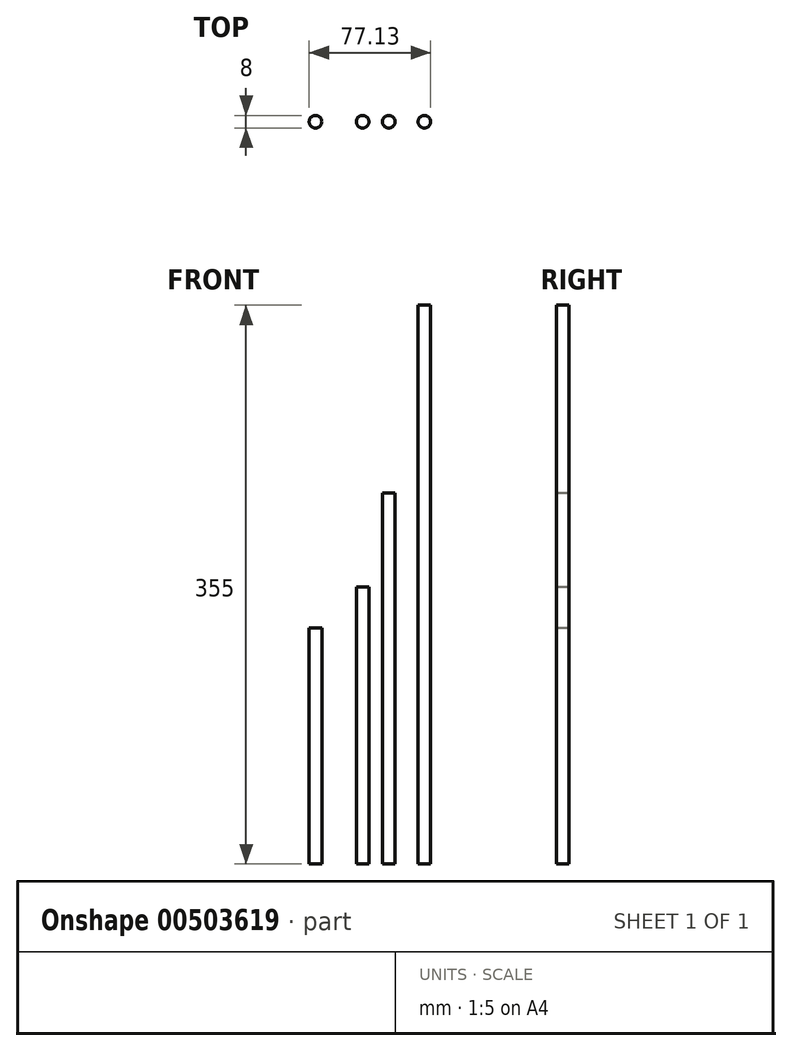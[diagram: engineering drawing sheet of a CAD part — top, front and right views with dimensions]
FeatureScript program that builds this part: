
annotation { "Feature Type Name" : "Feature", "Feature Type Description" : "" }
export const myFeature = defineFeature(function(context is Context, id is Id, definition is map)
    precondition{}
    {
        {
            var Q0;
            Q0=qCreatedBy(makeId("Top.planeOp"),FACE);
            var sketch = newSketch(context, id + "F0", { "sketchPlane" : qUnion([Q0])});
            skCircle(sketch, "E0", {"center": v(0, 0) * mm, "radius": 4 * mm});
            skCircle(sketch, "E1", {"center": v(16.6, 0) * mm, "radius": 4 * mm});
            skCircle(sketch, "E2", {"center": v(39.2, 0) * mm, "radius": 4 * mm});
            skSolve(sketch);
        }
        {
            var Q0;
            Q0=makeQuery(id+"F0.imprint","IMPRINT",FACE,{"disambiguationData":[TD([[makeQuery(id+"F0.imprint","IMPRINT",EDGE,{"derivedFrom":sQuery(id+"F0.wireOp",EDGE,"E0")}),1.0]])]});
            extrude(context, id + "F1", {"entities" : qUnion([Q0]), "offsetDistance" : 25 * mm, "depth" : 176 * mm});
        }
        {
            var Q0;
            Q0=makeQuery(id+"F0.imprint","IMPRINT",FACE,{"disambiguationData":[TD([[makeQuery(id+"F0.imprint","IMPRINT",EDGE,{"derivedFrom":sQuery(id+"F0.wireOp",EDGE,"E1")}),1.0]])]});
            extrude(context, id + "F2", {"entities" : qUnion([Q0]), "offsetDistance" : 25 * mm, "depth" : 235.7 * mm});
        }
        {
            var Q0;
            Q0=makeQuery(id+"F0.imprint","IMPRINT",FACE,{"disambiguationData":[TD([[makeQuery(id+"F0.imprint","IMPRINT",EDGE,{"derivedFrom":sQuery(id+"F0.wireOp",EDGE,"E2")}),1.0]])]});
            extrude(context, id + "F3", {"entities" : qUnion([Q0]), "depth" : 355 * mm});
        }
        {
            var Q0;
            Q0=qCreatedBy(makeId("Top.planeOp"),FACE);
            var sketch = newSketch(context, id + "F4", { "sketchPlane" : qUnion([Q0])});
            skCircle(sketch, "E3", {"center": v(-29.93, 0) * mm, "radius": 4 * mm});
            skSolve(sketch);
        }
        {
            var Q0;
            Q0=makeQuery(id+"F4.imprint","IMPRINT",FACE,{"disambiguationData":[TD([[makeQuery(id+"F4.imprint","IMPRINT",EDGE,{"derivedFrom":sQuery(id+"F4.wireOp",EDGE,"E3")}),1.0]])]});
            extrude(context, id + "F5", {"entities" : qUnion([Q0]), "depth" : 150 * mm, "offsetDistance" : 25 * mm});
        }
    });
